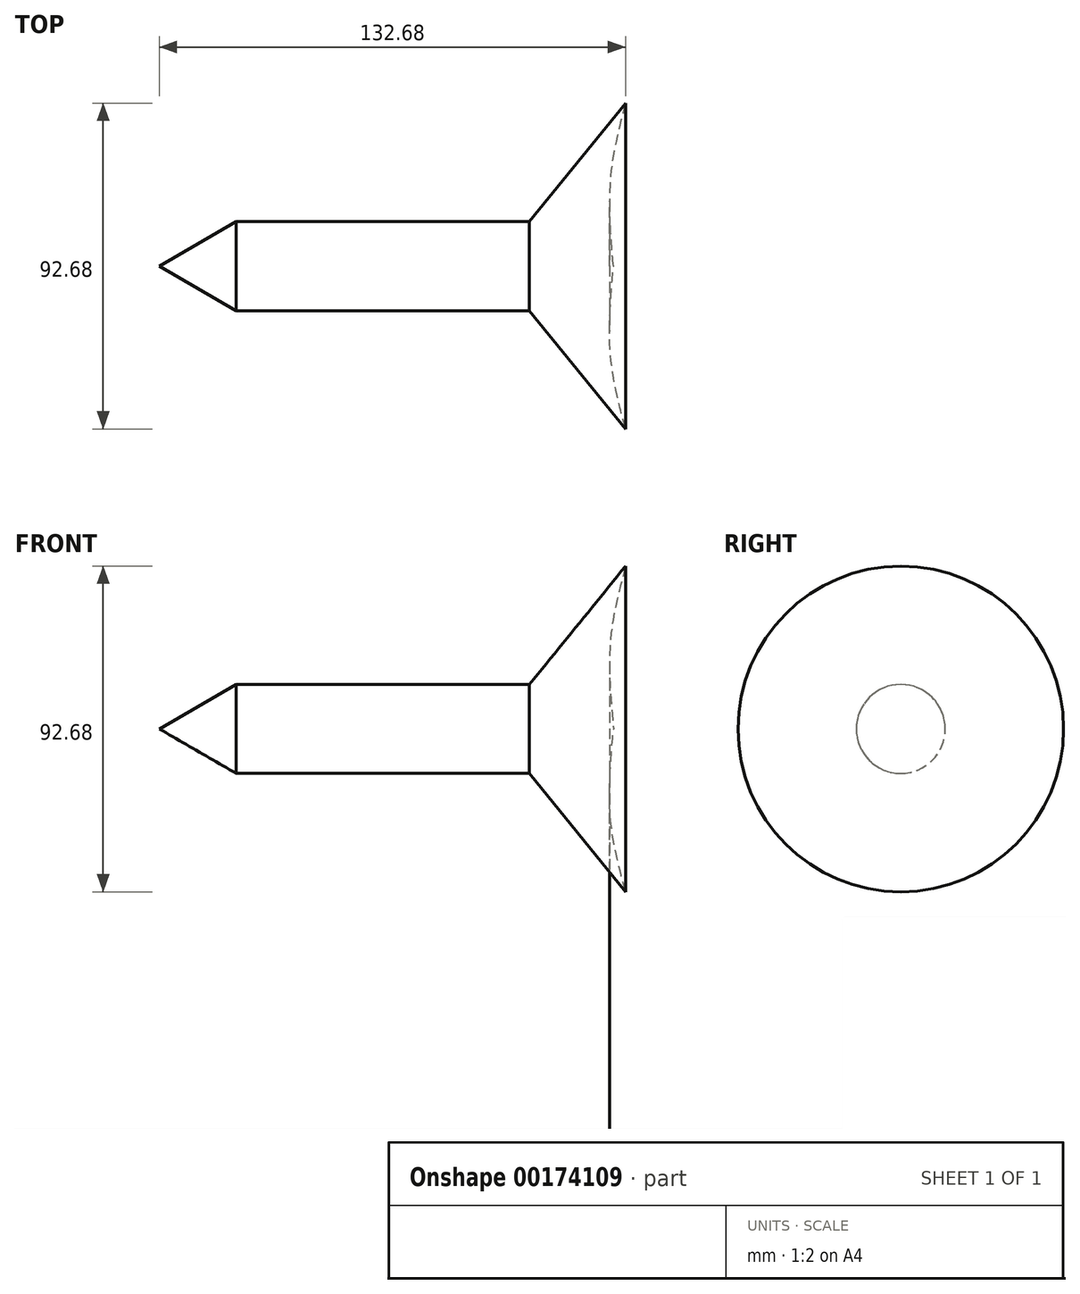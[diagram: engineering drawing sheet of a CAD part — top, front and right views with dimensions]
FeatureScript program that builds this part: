
annotation { "Feature Type Name" : "Feature", "Feature Type Description" : "" }
export const myFeature = defineFeature(function(context is Context, id is Id, definition is map)
    precondition{}
    {
        {
            var Q0;
            Q0=qCreatedBy(makeId("Front.planeOp"),FACE);
            var sketch = newSketch(context, id + "F0", { "sketchPlane" : qUnion([Q0])});
            skLineSegment(sketch, "E0", {"start": v(-61.16, 0) * mm, "end": v(-39.29, 12.66) * mm});
            skLineSegment(sketch, "E1", {"start": v(-39.29, 12.66) * mm, "end": v(44.18, 12.66) * mm});
            skLineSegment(sketch, "E2", {"start": v(44.18, 12.66) * mm, "end": v(71.52, 46.34) * mm});
            skFitSpline(sketch, "E3", {"points": [v(71.52, 46.34) * mm, v(67.2, 25.04) * mm, v(68.07, 0) * mm], "startDerivative": vector(-11.51, -43.15) * mm, "endDerivative": vector(4.42, -49.44) * mm});
            skLineSegment(sketch, "E4", {"start": v(-61.16, 0) * mm, "end": v(68.07, 0) * mm});
            skSolve(sketch);
        }
        {
            var Q0;
            Q0 = qSketchRegion(id + "F0", true);
            var Q1;
            Q1=sQuery(id+"F0.wireOp",EDGE,"E4");
            revolve(context, id + "F1", {"entities" : qUnion([Q0]), "axis" : qUnion([Q1]), "revolveType" : RevolveType.FULL});
        }
    });
